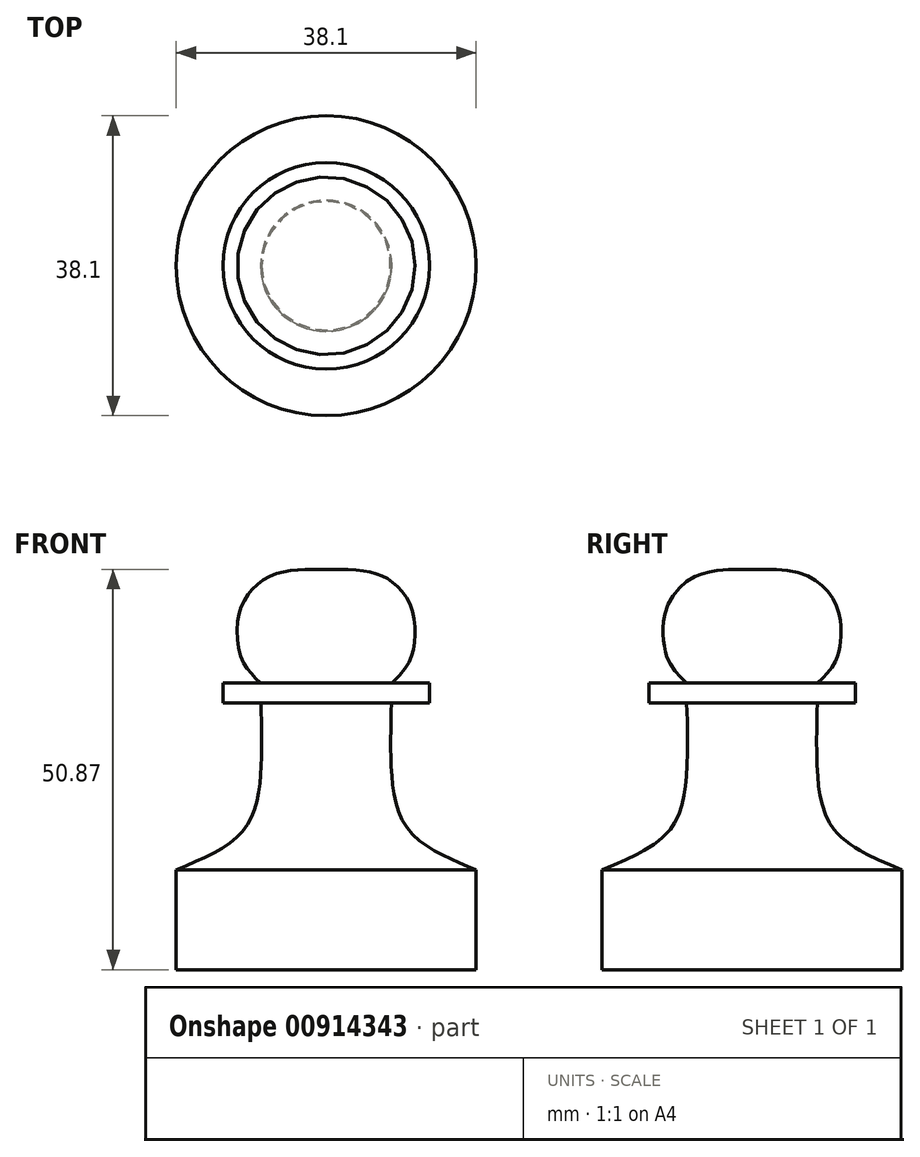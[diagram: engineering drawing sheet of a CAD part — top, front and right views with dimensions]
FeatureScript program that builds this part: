
annotation { "Feature Type Name" : "Feature", "Feature Type Description" : "" }
export const myFeature = defineFeature(function(context is Context, id is Id, definition is map)
    precondition{}
    {
        {
            var Q0;
            Q0=qCreatedBy(makeId("Front.planeOp"),FACE);
            var sketch = newSketch(context, id + "F0", { "sketchPlane" : qUnion([Q0])});
            skLineSegment(sketch, "E0", {"start": v(0, 0) * mm, "end": v(0, 50.8) * mm});
            skLineSegment(sketch, "E1", {"start": v(0, 0) * mm, "end": v(19.05, 0) * mm});
            skLineSegment(sketch, "E2", {"start": v(19.05, 0) * mm, "end": v(19.05, 12.7) * mm});
            skFitSpline(sketch, "E3", {"points": [v(19.05, 12.7) * mm, v(10.5, 17.71) * mm, v(8.3, 25.16) * mm, v(8.3, 33.92) * mm], "startDerivative": vector(-28.52, 11.63) * mm, "endDerivative": vector(0.8, 26.4) * mm});
            skLineSegment(sketch, "E4.bottom", {"start": v(0, 33.92) * mm, "end": v(13.12, 33.92) * mm});
            skLineSegment(sketch, "E4.top", {"start": v(0, 36.46) * mm, "end": v(13.12, 36.46) * mm});
            skLineSegment(sketch, "E4.left", {"start": v(0, 33.92) * mm, "end": v(0, 36.46) * mm});
            skLineSegment(sketch, "E4.right", {"start": v(13.12, 33.92) * mm, "end": v(13.12, 36.46) * mm});
            skFitSpline(sketch, "E5", {"points": [v(8.34, 36.46) * mm, v(11.12, 40.98) * mm, v(10.82, 46) * mm, v(8.26, 49.34) * mm, v(5.24, 50.58) * mm, v(0, 50.8) * mm], "startDerivative": vector(27.4, 24.52) * mm, "endDerivative": vector(-24.48, -1.93) * mm});
            skSolve(sketch);
        }
        {
            var Q0;
            {var subQ7=sQuery(id+"F0.wireOp",EDGE,"E4.right");Q0=makeQuery(id+"F0.imprint","IMPRINT",FACE,{"disambiguationData":[TD([[makeQuery(id+"F0.imprint","IMPRINT",EDGE,{"derivedFrom":subQ7}),1.0]])]});}
            var Q1;
            {var subQ0=sQuery(id+"F0.wireOp",EDGE,"E1");Q1=makeQuery(id+"F0.imprint","IMPRINT",FACE,{"disambiguationData":[TD([[makeQuery(id+"F0.imprint","IMPRINT",EDGE,{"derivedFrom":subQ0}),1.0]])]});}
            var Q2;
            {var subQ3=sQuery(id+"F0.wireOp",EDGE,"E5");Q2=makeQuery(id+"F0.imprint","IMPRINT",FACE,{"disambiguationData":[TD([[makeQuery(id+"F0.imprint","IMPRINT",EDGE,{"derivedFrom":subQ3}),1.0]])]});}
            var Q3;
            Q3=sQuery(id+"F0.wireOp",EDGE,"E0");
            revolve(context, id + "F1", {"surfaceOperationType" : NewSurfaceOperationType.NEW, "entities" : qUnion([Q0, Q1, Q2]), "axis" : qUnion([Q3]), "revolveType" : RevolveType.FULL});
        }
    });
